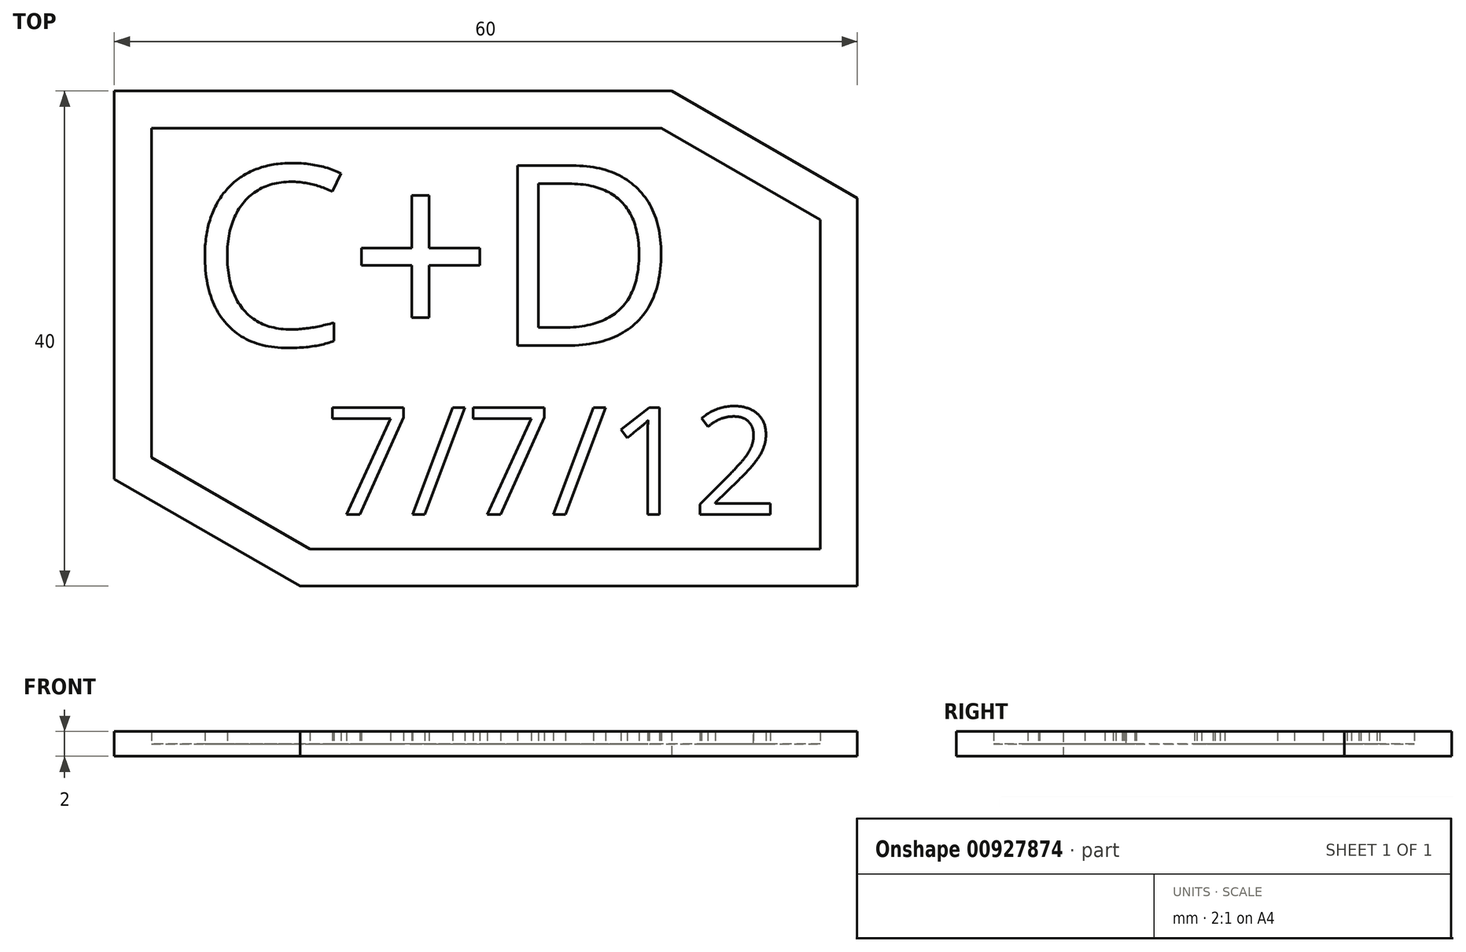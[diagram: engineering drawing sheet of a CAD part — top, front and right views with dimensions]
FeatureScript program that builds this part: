
annotation { "Feature Type Name" : "Feature", "Feature Type Description" : "" }
export const myFeature = defineFeature(function(context is Context, id is Id, definition is map)
    precondition{}
    {
        {
            var Q0;
            Q0=qCreatedBy(makeId("Top.planeOp"),FACE);
            var sketch = newSketch(context, id + "F0", { "sketchPlane" : qUnion([Q0])});
            skLineSegment(sketch, "E0.bottom", {"start": v(0, 0) * mm, "end": v(60, 0) * mm});
            skLineSegment(sketch, "E0.top", {"start": v(0, 40) * mm, "end": v(60, 40) * mm});
            skLineSegment(sketch, "E0.left", {"start": v(0, 0) * mm, "end": v(0, 40) * mm});
            skLineSegment(sketch, "E0.right", {"start": v(60, 0) * mm, "end": v(60, 40) * mm});
            skSolve(sketch);
        }
        {
            var Q0;
            Q0=makeQuery(id+"F0.imprint","IMPRINT",FACE,{"disambiguationData":[TD([[makeQuery(id+"F0.imprint","IMPRINT",EDGE,{"derivedFrom":sQuery(id+"F0.wireOp",EDGE,"E0.bottom")}),1.0]])]});
            extrude(context, id + "F1", {"entities" : qUnion([Q0]), "depth" : 1 * mm, "offsetDistance" : 25 * mm});
        }
        {
            var Q0;
            Q0=makeQuery(id+"F1.opExtrude","SWEPT_EDGE",EDGE,{"disambiguationData":[OSD([sQuery(id+"F0.wireOp",EDGE,"E0.bottom"),sQuery(id+"F0.wireOp",EDGE,"E0.left")])]});
            var Q1;
            Q1=makeQuery(id+"F1.opExtrude","SWEPT_EDGE",EDGE,{"disambiguationData":[OSD([sQuery(id+"F0.wireOp",EDGE,"E0.top"),sQuery(id+"F0.wireOp",EDGE,"E0.right")])]});
            chamfer(context, id + "F2", {"entities" : qUnion([Q0, Q1]), "chamferType" : ChamferType.OFFSET_ANGLE, "width" : 15 * mm, "oppositeDirection" : false, "angle" : 30 * degree, "tangentPropagation" : true});
        }
        {
            var Q0;
            Q0=makeQuery(id+"F1.opExtrude","CAP_FACE",FACE,{"disambiguationData":[OSD([sQuery(id+"F0.wireOp",EDGE,"E0.bottom"),sQuery(id+"F0.wireOp",EDGE,"E0.top"),sQuery(id+"F0.wireOp",EDGE,"E0.left"),sQuery(id+"F0.wireOp",EDGE,"E0.right")])],"isStart":false});
            var sketch = newSketch(context, id + "F3", { "sketchPlane" : qUnion([Q0])});
            skLineSegment(sketch, "E1.0.0", {"start": v(60, 0) * mm, "end": v(60, 31.34) * mm});
            skLineSegment(sketch, "E1.0.1", {"start": v(60, 31.34) * mm, "end": v(45, 40) * mm});
            skLineSegment(sketch, "E1.0.2", {"start": v(45, 40) * mm, "end": v(0, 40) * mm});
            skLineSegment(sketch, "E1.0.3", {"start": v(0, 40) * mm, "end": v(0, 8.66) * mm});
            skLineSegment(sketch, "E1.0.4", {"start": v(0, 8.66) * mm, "end": v(15, 0) * mm});
            skLineSegment(sketch, "E1.0.5", {"start": v(15, 0) * mm, "end": v(60, 0) * mm});
            skLineSegment(sketch, "E2.0", {"start": v(15.8, 3) * mm, "end": v(57, 3) * mm});
            skLineSegment(sketch, "E2.1", {"start": v(57, 29.6) * mm, "end": v(44.2, 37) * mm});
            skLineSegment(sketch, "E2.2", {"start": v(44.2, 37) * mm, "end": v(3, 37) * mm});
            skLineSegment(sketch, "E2.3", {"start": v(57, 3) * mm, "end": v(57, 29.6) * mm});
            skLineSegment(sketch, "E2.4", {"start": v(3, 37) * mm, "end": v(3, 10.4) * mm});
            skLineSegment(sketch, "E2.5", {"start": v(3, 10.4) * mm, "end": v(15.8, 3) * mm});
            skSolve(sketch);
        }
        {
            var Q0;
            Q0=makeQuery(id+"F3.imprint","IMPRINT",FACE,{"disambiguationData":[TD([[makeQuery(id+"F3.imprint","IMPRINT",EDGE,{"derivedFrom":sQuery(id+"F3.wireOp",EDGE,"E1.0.0")}),1.0]])]});
            extrude(context, id + "F4", {"entities" : qUnion([Q0]), "operationType" : NewBodyOperationType.ADD, "depth" : 1 * mm, "offsetDistance" : 25 * mm});
        }
        {
            var Q0;
            Q0=makeQuery(id+"F1.opExtrude","CAP_FACE",FACE,{"disambiguationData":[OSD([sQuery(id+"F0.wireOp",EDGE,"E0.bottom"),sQuery(id+"F0.wireOp",EDGE,"E0.top"),sQuery(id+"F0.wireOp",EDGE,"E0.left"),sQuery(id+"F0.wireOp",EDGE,"E0.right")])],"isStart":false});
            var sketch = newSketch(context, id + "F5", { "sketchPlane" : qUnion([Q0])});
            skText(sketch, "E3", { "text": "C+D", "fontName": "OpenSans-Regular.ttf"});
            skText(sketch, "E4", { "text": "7/7/12", "fontName": "OpenSans-Regular.ttf"});
            const initialGuessF5  = {"E3": [0.00607, 0.01944, 1, 0, 0.01466], "E4": [0.01705, 0.00578, 1, 0, 0.00872]};
            skSetInitialGuess(sketch, initialGuessF5);
            skSolve(sketch);
        }
        {
            var Q0;
            Q0 = qSketchRegion(id + "F5", true);
            extrude(context, id + "F6", {"entities" : qUnion([Q0]), "operationType" : NewBodyOperationType.ADD, "depth" : 1 * mm, "offsetDistance" : 25 * mm});
        }
    });
